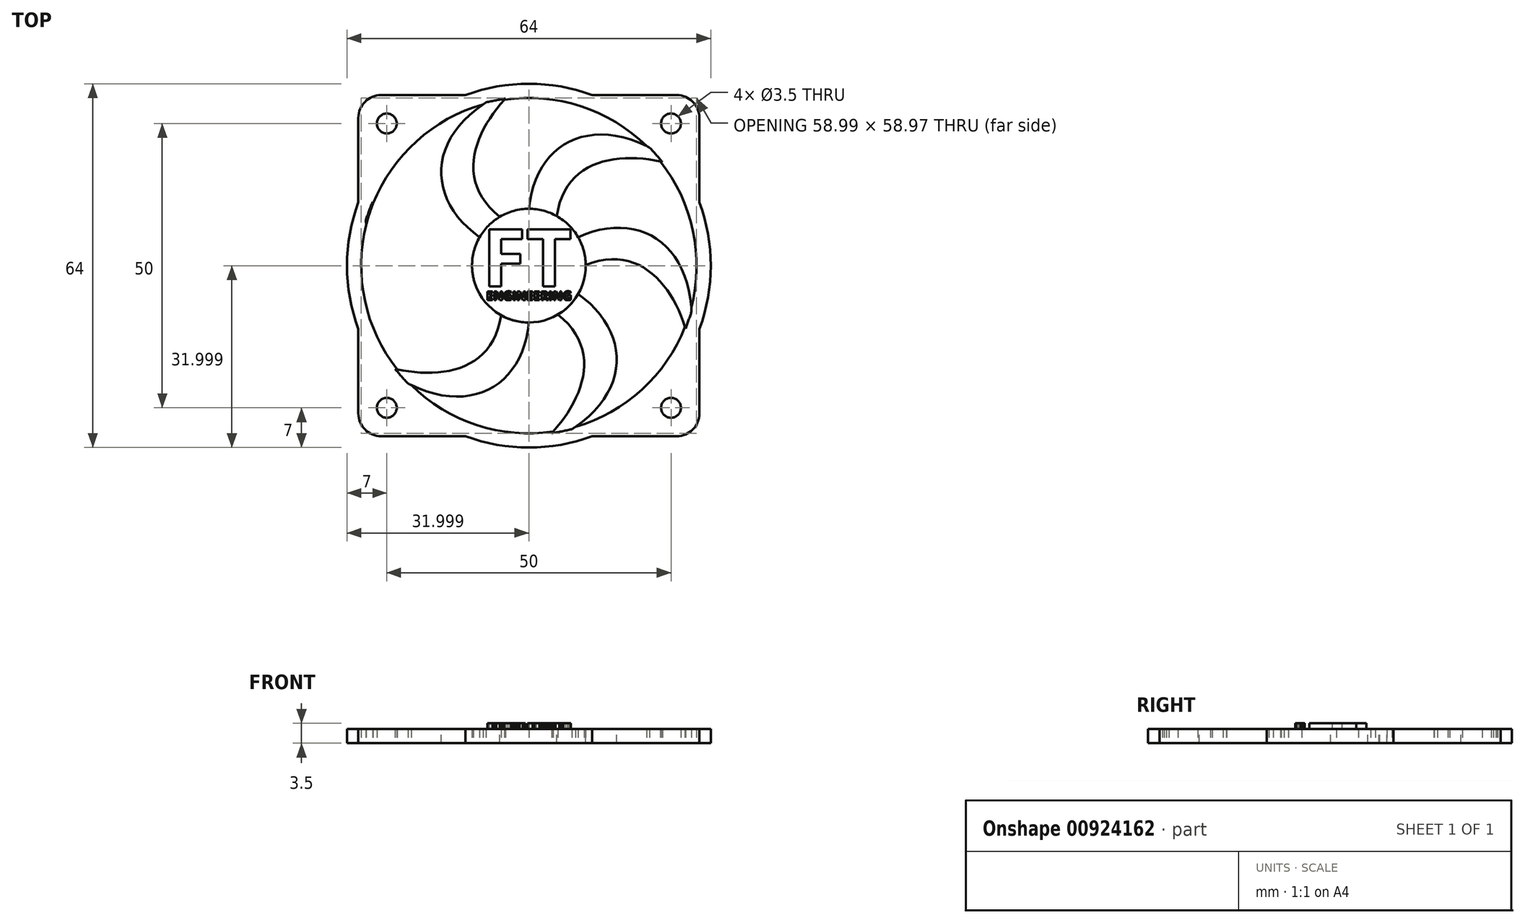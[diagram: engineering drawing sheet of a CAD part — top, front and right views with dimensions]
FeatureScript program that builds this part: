
annotation { "Feature Type Name" : "Feature", "Feature Type Description" : "" }
export const myFeature = defineFeature(function(context is Context, id is Id, definition is map)
    precondition{}
    {
        {
            var Q0;
            Q0=qCreatedBy(makeId("Top.planeOp"),FACE);
            var sketch = newSketch(context, id + "F0", { "sketchPlane" : qUnion([Q0])});
            skLineSegment(sketch, "E0.bottom", {"start": v(26, 30) * mm, "end": v(-26, 30) * mm});
            skLineSegment(sketch, "E0.top", {"start": v(26, -30) * mm, "end": v(-26, -30) * mm});
            skLineSegment(sketch, "E0.left", {"start": v(30, 26) * mm, "end": v(30, -26) * mm});
            skLineSegment(sketch, "E0.right", {"start": v(-30, 26) * mm, "end": v(-30, -26) * mm});
            skPoint(sketch, "E1.visualSharp", {"position": v(-30, 30) * mm});
            skArc(sketch, "E1.filletArc", {"start": v(-26, 30) * mm, "mid": v(-28.83, 28.83) * mm, "end": v(-30, 26) * mm});
            skPoint(sketch, "E2.visualSharp", {"position": v(30, 30) * mm});
            skArc(sketch, "E2.filletArc", {"start": v(30, 26) * mm, "mid": v(28.83, 28.83) * mm, "end": v(26, 30) * mm});
            skPoint(sketch, "E3.visualSharp", {"position": v(30, -30) * mm});
            skArc(sketch, "E3.filletArc", {"start": v(26, -30) * mm, "mid": v(28.83, -28.83) * mm, "end": v(30, -26) * mm});
            skPoint(sketch, "E4.visualSharp", {"position": v(-30, -30) * mm});
            skArc(sketch, "E4.filletArc", {"start": v(-30, -26) * mm, "mid": v(-28.83, -28.83) * mm, "end": v(-26, -30) * mm});
            skPoint(sketch, "E5", {"position": v(-25, 25) * mm});
            skPoint(sketch, "E6", {"position": v(25, 25) * mm});
            skPoint(sketch, "E7", {"position": v(25, -25) * mm});
            skPoint(sketch, "E8", {"position": v(-25, -25) * mm});
            skCircle(sketch, "E9", {"center": v(25, -25) * mm, "radius": 1.75 * mm});
            skCircle(sketch, "E10", {"center": v(0, 0) * mm, "radius": 32 * mm});
            skCircle(sketch, "E11", {"center": v(0, 0) * mm, "radius": 29.5 * mm});
            skCircle(sketch, "E12", {"center": v(0, 0) * mm, "radius": 10 * mm});
            skCircle(sketch, "E13", {"center": v(-25, -25) * mm, "radius": 1.75 * mm});
            skCircle(sketch, "E14", {"center": v(-25, 25) * mm, "radius": 1.75 * mm});
            skCircle(sketch, "E15", {"center": v(25, 25) * mm, "radius": 1.75 * mm});
            skFitSpline(sketch, "E16", {"points": [v(0, 10) * mm, v(21.24, 20.76) * mm], "startDerivative": vector(3.08, 33.24) * mm, "endDerivative": vector(33.2, -17.1) * mm});
            skFitSpline(sketch, "E17", {"points": [v(4.9, 8.72) * mm, v(23.48, 18.25) * mm], "startDerivative": vector(4.47, 30.14) * mm, "endDerivative": vector(23.41, -5.27) * mm});
            skArc(sketch, "E18", {"start": v(4.9, 8.72) * mm, "mid": v(2.53, 9.67) * mm, "end": v(0, 10) * mm});
            skArc(sketch, "E19", {"start": v(23.48, 18.25) * mm, "mid": v(22.38, 19.52) * mm, "end": v(21.24, 20.76) * mm});
            skPoint(sketch, "E20", {"position": v(8.66, 5) * mm});
            skLineSegment(sketch, "E21", {"start": v(0, 10) * mm, "end": v(0, 0) * mm, "construction": true});
            skLineSegment(sketch, "E22", {"start": v(0, 0) * mm, "end": v(8.66, 5) * mm, "construction": true});
            skPoint(sketch, "E23", {"position": v(8.66, -5) * mm});
            skLineSegment(sketch, "E24", {"start": v(0, 0) * mm, "end": v(8.66, -5) * mm, "construction": true});
            skPoint(sketch, "E25", {"position": v(0, -10) * mm});
            skPoint(sketch, "E26", {"position": v(-8.66, -5) * mm});
            skPoint(sketch, "E27", {"position": v(-8.66, 5) * mm});
            skLineSegment(sketch, "E28", {"start": v(0, 0) * mm, "end": v(-8.66, 5) * mm, "construction": true});
            skLineSegment(sketch, "E29", {"start": v(0, 0) * mm, "end": v(-8.66, -5) * mm, "construction": true});
            skLineSegment(sketch, "E30", {"start": v(0, 0) * mm, "end": v(0, -10) * mm, "construction": true});
            skFitSpline(sketch, "E31", {"points": [v(8.66, 5) * mm, v(28.61, -8.07) * mm], "startDerivative": vector(30.33, 13.95) * mm, "endDerivative": vector(1.8, -37.3) * mm});
            skFitSpline(sketch, "E32", {"points": [v(10, 0.12) * mm, v(27.56, -11.06) * mm], "startDerivative": vector(28.34, 11.2) * mm, "endDerivative": vector(7.14, -22.91) * mm});
            skArc(sketch, "E33", {"start": v(10, 0.12) * mm, "mid": v(9.64, 2.65) * mm, "end": v(8.66, 5) * mm});
            skArc(sketch, "E34", {"start": v(27.56, -11.06) * mm, "mid": v(28.1, -9.57) * mm, "end": v(28.61, -8.07) * mm});
            skFitSpline(sketch, "E35", {"points": [v(8.66, -5) * mm, v(7.55, -28.77) * mm], "startDerivative": vector(27.25, -19.29) * mm, "endDerivative": vector(-31.4, -20.21) * mm});
            skFitSpline(sketch, "E36", {"points": [v(5.1, -8.6) * mm, v(4, -29.48) * mm], "startDerivative": vector(23.87, -18.94) * mm, "endDerivative": vector(-16.27, -17.64) * mm});
            skArc(sketch, "E37", {"start": v(5.1, -8.6) * mm, "mid": v(7.11, -7.03) * mm, "end": v(8.66, -5) * mm});
            skArc(sketch, "E38", {"start": v(4, -29.48) * mm, "mid": v(5.78, -29.15) * mm, "end": v(7.55, -28.77) * mm});
            skFitSpline(sketch, "E39", {"points": [v(0, -10) * mm, v(-21.26, -20.74) * mm], "startDerivative": vector(-3.08, -33.24) * mm, "endDerivative": vector(-33.2, 17.1) * mm});
            skFitSpline(sketch, "E40", {"points": [v(-4.9, -8.72) * mm, v(-23.55, -18.16) * mm], "startDerivative": vector(-4.47, -30.14) * mm, "endDerivative": vector(-23.41, 5.27) * mm});
            skArc(sketch, "E41", {"start": v(-4.9, -8.72) * mm, "mid": v(-2.53, -9.67) * mm, "end": v(0, -10) * mm});
            skArc(sketch, "E42", {"start": v(-23.55, -18.16) * mm, "mid": v(-22.42, -19.47) * mm, "end": v(-21.26, -20.74) * mm});
            skFitSpline(sketch, "E43", {"points": [v(-8.66, -5) * mm, v(-28.68, 7.99) * mm], "startDerivative": vector(-30.33, -13.95) * mm, "endDerivative": vector(-1.8, 37.3) * mm});
            skFitSpline(sketch, "E44", {"points": [v(-10, -0.12) * mm, v(-27.5, 11.23) * mm], "startDerivative": vector(-28.34, -11.2) * mm, "endDerivative": vector(-7.14, 22.91) * mm});
            skArc(sketch, "E45", {"start": v(-10, -0.12) * mm, "mid": v(-9.64, -2.65) * mm, "end": v(-8.66, -5) * mm});
            skArc(sketch, "E46", {"start": v(-27.5, 11.23) * mm, "mid": v(-28.11, 9.62) * mm, "end": v(-28.68, 7.99) * mm});
            skFitSpline(sketch, "E47", {"points": [v(-8.66, 5) * mm, v(-7.53, 28.72) * mm], "startDerivative": vector(-27.25, 19.29) * mm, "endDerivative": vector(31.4, 20.21) * mm});
            skFitSpline(sketch, "E48", {"points": [v(-5.1, 8.6) * mm, v(-4.12, 29.38) * mm], "startDerivative": vector(-23.87, 18.94) * mm, "endDerivative": vector(16.27, 17.64) * mm});
            skArc(sketch, "E49", {"start": v(-5.1, 8.6) * mm, "mid": v(-7.11, 7.03) * mm, "end": v(-8.66, 5) * mm});
            skArc(sketch, "E50", {"start": v(-4.12, 29.38) * mm, "mid": v(-5.83, 29.08) * mm, "end": v(-7.53, 28.72) * mm});
            skSolve(sketch);
        }
        {
            var Q0;
            {var subQ5=sQuery(id+"F0.wireOp",EDGE,"E1.filletArc");Q0=makeQuery(id+"F0.imprint","IMPRINT",FACE,{"disambiguationData":[TD([[makeQuery(id+"F0.imprint","IMPRINT",EDGE,{"derivedFrom":subQ5}),1.0]])]});}
            var Q1;
            {var subQ4=sQuery(id+"F0.wireOp",EDGE,"E10");var subQ5=sQuery(id+"F0.wireOp",EDGE,"E0.bottom");var subQ9=makeQuery(id+"F0.imprint","INTERSECT",VERTEX,{"disambiguationData":[OD(0.0)],"derivedFrom":[subQ5,subQ4]});Q1=makeQuery(id+"F0.imprint","IMPRINT",FACE,{"disambiguationData":[TD([[makeQuery(id+"F0.imprint","IMPRINT",EDGE,{"disambiguationData":[TD([[subQ9,-1.0]])],"derivedFrom":subQ5}),1.0]])]});}
            var Q2;
            {var subQ0=sQuery(id+"F0.wireOp",EDGE,"E10");var subQ1=sQuery(id+"F0.wireOp",EDGE,"E0.bottom");var subQ2=makeQuery(id+"F0.imprint","INTERSECT",VERTEX,{"disambiguationData":[OD(0.0)],"derivedFrom":[subQ1,subQ0]});Q2=makeQuery(id+"F0.imprint","IMPRINT",FACE,{"disambiguationData":[TD([[makeQuery(id+"F0.imprint","IMPRINT",EDGE,{"disambiguationData":[TD([[subQ2,-1.0]])],"derivedFrom":subQ1}),-1.0]])]});}
            var Q3;
            {var subQ5=sQuery(id+"F0.wireOp",EDGE,"E2.filletArc");Q3=makeQuery(id+"F0.imprint","IMPRINT",FACE,{"disambiguationData":[TD([[makeQuery(id+"F0.imprint","IMPRINT",EDGE,{"derivedFrom":subQ5}),1.0]])]});}
            var Q4;
            {var subQ0=sQuery(id+"F0.wireOp",EDGE,"E10");var subQ1=sQuery(id+"F0.wireOp",EDGE,"E0.left");var subQ2=makeQuery(id+"F0.imprint","INTERSECT",VERTEX,{"disambiguationData":[OD(0.0)],"derivedFrom":[subQ1,subQ0]});Q4=makeQuery(id+"F0.imprint","IMPRINT",FACE,{"disambiguationData":[TD([[makeQuery(id+"F0.imprint","IMPRINT",EDGE,{"disambiguationData":[TD([[subQ2,-1.0]])],"derivedFrom":subQ1}),1.0]])]});}
            var Q5;
            {var subQ0=sQuery(id+"F0.wireOp",EDGE,"E3.filletArc");Q5=makeQuery(id+"F0.imprint","IMPRINT",FACE,{"disambiguationData":[TD([[makeQuery(id+"F0.imprint","IMPRINT",EDGE,{"derivedFrom":subQ0}),1.0]])]});}
            var Q6;
            {var subQ0=sQuery(id+"F0.wireOp",EDGE,"E10");var subQ1=sQuery(id+"F0.wireOp",EDGE,"E0.top");var subQ2=makeQuery(id+"F0.imprint","INTERSECT",VERTEX,{"disambiguationData":[OD(0.0)],"derivedFrom":[subQ1,subQ0]});Q6=makeQuery(id+"F0.imprint","IMPRINT",FACE,{"disambiguationData":[TD([[makeQuery(id+"F0.imprint","IMPRINT",EDGE,{"disambiguationData":[TD([[subQ2,-1.0]])],"derivedFrom":subQ1}),1.0]])]});}
            var Q7;
            {var subQ5=sQuery(id+"F0.wireOp",EDGE,"E4.filletArc");Q7=makeQuery(id+"F0.imprint","IMPRINT",FACE,{"disambiguationData":[TD([[makeQuery(id+"F0.imprint","IMPRINT",EDGE,{"derivedFrom":subQ5}),1.0]])]});}
            var Q8;
            {var subQ0=sQuery(id+"F0.wireOp",EDGE,"E10");var subQ1=sQuery(id+"F0.wireOp",EDGE,"E0.right");var subQ2=makeQuery(id+"F0.imprint","INTERSECT",VERTEX,{"disambiguationData":[OD(0.0)],"derivedFrom":[subQ1,subQ0]});Q8=makeQuery(id+"F0.imprint","IMPRINT",FACE,{"disambiguationData":[TD([[makeQuery(id+"F0.imprint","IMPRINT",EDGE,{"disambiguationData":[TD([[subQ2,-1.0]])],"derivedFrom":subQ1}),-1.0]])]});}
            extrude(context, id + "F1", {"entities" : qUnion([Q0, Q1, Q2, Q3, Q4, Q5, Q6, Q7, Q8]), "depth" : 2.5 * mm, "offsetDistance" : 25 * mm});
        }
        {
            var Q0;
            {var subQ0=sQuery(id+"F0.wireOp",EDGE,"E12");var subQ5=makeQuery(id+"F0.imprint","INTERSECT",VERTEX,{"derivedFrom":[subQ0,sQuery(id+"F0.wireOp",EDGE,"f35b7cc9-3e88-4b27-bd39-567b3a4cbca4")]});Q0=makeQuery(id+"F0.imprint","IMPRINT",FACE,{"disambiguationData":[TD([[makeQuery(id+"F0.imprint","IMPRINT",EDGE,{"disambiguationData":[TD([[subQ5,-1.0]])],"derivedFrom":subQ0}),1.0]])]});}
            extrude(context, id + "F2", {"entities" : qUnion([Q0]), "depth" : 2.5 * mm, "offsetDistance" : 25 * mm});
        }
        {
            var Q0;
            {var subQ0=sQuery(id+"F0.wireOp",EDGE,"E16");Q0=makeQuery(id+"F0.imprint","IMPRINT",FACE,{"disambiguationData":[TD([[makeQuery(id+"F0.imprint","IMPRINT",EDGE,{"derivedFrom":subQ0}),-1.0]])]});}
            var Q1;
            {var subQ0=sQuery(id+"F0.wireOp",EDGE,"E31");Q1=makeQuery(id+"F0.imprint","IMPRINT",FACE,{"disambiguationData":[TD([[makeQuery(id+"F0.imprint","IMPRINT",EDGE,{"derivedFrom":subQ0}),-1.0]])]});}
            var Q2;
            {var subQ0=sQuery(id+"F0.wireOp",EDGE,"E35");Q2=makeQuery(id+"F0.imprint","IMPRINT",FACE,{"disambiguationData":[TD([[makeQuery(id+"F0.imprint","IMPRINT",EDGE,{"derivedFrom":subQ0}),-1.0]])]});}
            var Q3;
            {var subQ0=sQuery(id+"F0.wireOp",EDGE,"E39");Q3=makeQuery(id+"F0.imprint","IMPRINT",FACE,{"disambiguationData":[TD([[makeQuery(id+"F0.imprint","IMPRINT",EDGE,{"derivedFrom":subQ0}),-1.0]])]});}
            var Q4;
            {var subQ0=sQuery(id+"F0.wireOp",EDGE,"E43");Q4=makeQuery(id+"F0.imprint","IMPRINT",FACE,{"disambiguationData":[TD([[makeQuery(id+"F0.imprint","IMPRINT",EDGE,{"derivedFrom":subQ0}),-1.0]])]});}
            var Q5;
            {var subQ0=sQuery(id+"F0.wireOp",EDGE,"E47");Q5=makeQuery(id+"F0.imprint","IMPRINT",FACE,{"disambiguationData":[TD([[makeQuery(id+"F0.imprint","IMPRINT",EDGE,{"derivedFrom":subQ0}),-1.0]])]});}
            extrude(context, id + "F3", {"entities" : qUnion([Q0, Q1, Q2, Q3, Q4, Q5]), "depth" : 2.5 * mm, "offsetDistance" : 25 * mm});
        }
        {
            var Q0;
            Q0=makeQuery(id+"F2.opExtrude","CAP_FACE",FACE,{"disambiguationData":[OSD([sQuery(id+"F0.wireOp",EDGE,"E12")])],"isStart":false});
            cPlane(context, id + "F4", {"entities" : qUnion([Q0]), "cplaneType" : CPlaneType.OFFSET, "offset" : 0 * mm, "width" : 150 * mm, "height" : 150 * mm});
        }
        {
            var Q0;
            Q0=qCreatedBy(id+"F4.planeOp",FACE);
            var sketch = newSketch(context, id + "F5", { "sketchPlane" : qUnion([Q0])});
            skText(sketch, "E51", { "text": "FT", "fontName": "OpenSans-Bold.ttf"});
            skText(sketch, "E52", { "text": "ENGINEERING", "fontName": "OpenSans-Bold.ttf"});
            const initialGuessF5  = {"E51": [-0.00825, -0.00363, 1, 0, 0.01013], "E52": [-0.0075, -0.00607, 1, 0, 0.00157]};
            skSetInitialGuess(sketch, initialGuessF5);
            skSolve(sketch);
        }
        {
            var Q0;
            Q0 = qSketchRegion(id + "F5", true);
            extrude(context, id + "F6", {"entities" : qUnion([Q0]), "operationType" : NewBodyOperationType.ADD, "depth" : 1 * mm, "offsetDistance" : 25 * mm});
        }
    });
